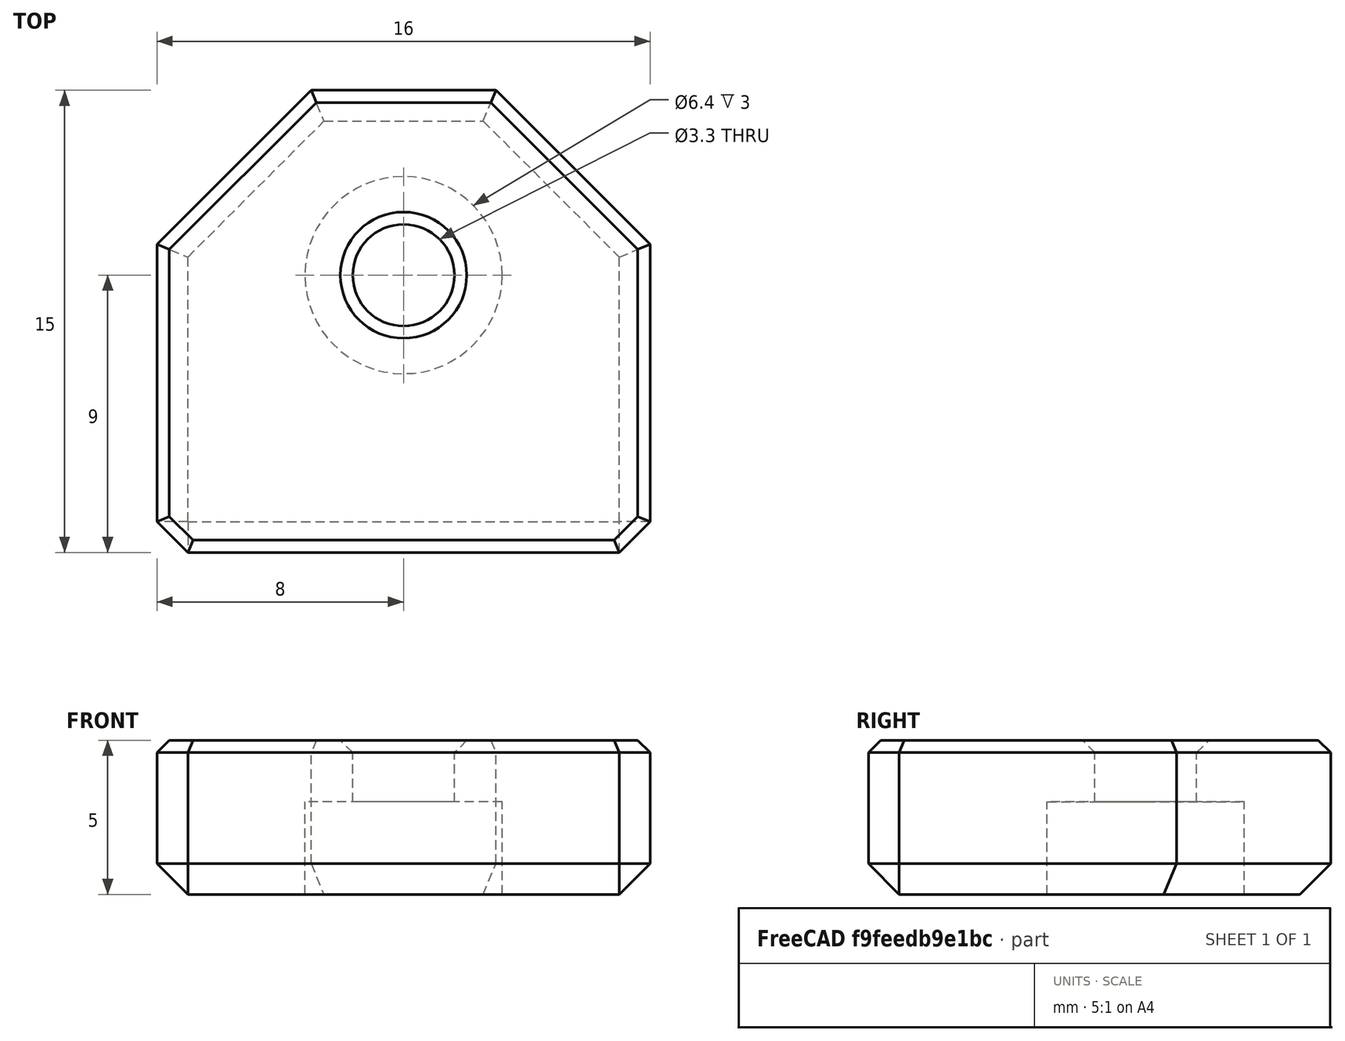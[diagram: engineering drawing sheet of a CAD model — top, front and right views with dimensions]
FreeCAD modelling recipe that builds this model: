
FCSTD DOCUMENT  (FreeCAD 0.18R16146 (Git))
Label: rail-stopper
License: Other
LicenseURL: GPL3
objects: Part::Chamfer×3, Part::Cylinder×2, Part::Box×1, Part::MultiFuse×1, Part::Cut×1
note: 8 computed .brp shape members not serialized (recipe doc carries the construction recipe); baked Part::Feature solids carry a one-line shape summary decoded from their .brp

FEATURE [Part::Box] Box001  label="Cube001"
  AttacherType = Attacher::AttachEngine3D
  Height = 5
  Length = 16
  Placement = pos=(-8,0,0) rot=(0,0,1;0rad)
  Width = 15
FEATURE [Part::Cylinder] Cylinder
  Angle = 360
  AttacherType = Attacher::AttachEngine3D
  Height = 4
  Placement = pos=(0,9,0) rot=(0,0,1;0rad)
  Radius = 3.2
FEATURE [Part::Cylinder] Cylinder001
  Angle = 360
  AttacherType = Attacher::AttachEngine3D
  Height = 10
  Placement = pos=(0,9,0) rot=(0,0,1;0rad)
  Radius = 1.65
FEATURE [Part::MultiFuse] Fusion
  Placement = pos=(0,0,-1) rot=(0,0,1;0rad)
  Shapes = -> [Cylinder,Cylinder001]
FEATURE [Part::Cut] Cut
  Base = -> Box001
  Tool = -> Fusion
FEATURE [Part::Chamfer] Chamfer
  Base = -> Cut
  Edges = 2 edges r=5: [Edge3,Edge12]
FEATURE [Part::Chamfer] Chamfer001
  Base = -> Chamfer
  Edges = 8 edges r=1: [Edge3,Edge4,Edge11,Edge13,Edge14,Edge15,Edge16,Edge17]
FEATURE [Part::Chamfer] Chamfer002
  Base = -> Chamfer001
  Edges = 9 edges r=0.4: [Edge1,Edge5,Edge6,Edge7,Edge8,Edge9,Edge10,Edge11,Edge12]
